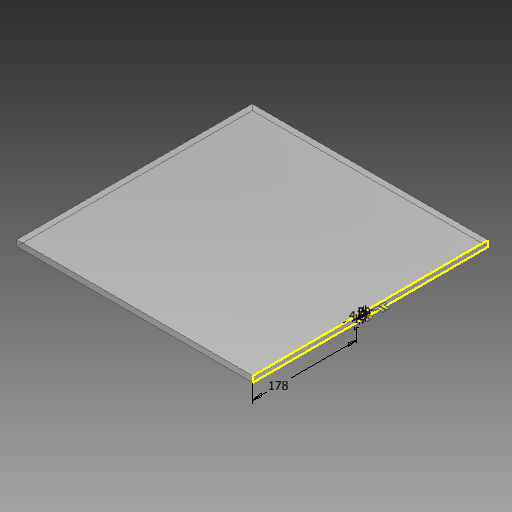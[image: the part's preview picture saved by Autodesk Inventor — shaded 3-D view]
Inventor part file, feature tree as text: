
AUTODESK INVENTOR PART (.ipt)
format: ipt  version: 2018 (Build 220112000, 112)  size: 162,816 bytes
history: native  units: mm
features: extrude x3, sketch x2, pattern_linear x1, projected_geometry x1
ambient origin geometry x8: Origin, YZ Plane, XZ Plane, XY Plane, X Axis, Y Axis, Z Axis, Center Point
bodies: Volumenkörper1 (feature_tree)
feature tree (7):
  extrude  "Extrusion1"  Depth=400.0mm
  sketch  "Skizze2"  dims[d2=10.0mm d3=0.0mm d4=20.0mm d5=1.0mm d6=11.0mm d7=2.0mm d8=4.5mm d10=178.0mm d11=4.0mm d12=0.0mm d15=13.0mm d16=0.0mm d17=20.0mm d19=27.0mm]
  extrude  "Extrusion2"  Depth=20.0mm
  extrude  "Extrusion4"  Depth=1.0mm
  pattern_linear  "Rechteckige Anordnung1"  Spacing1=11.0mm  [1 undecoded]
  sketch  "Skizze1"  dims[d0=400.0mm d1=400.0mm]
  projected_geometry  "Projizierte Kontur1"
note: 1 required parameter value undecoded (feature->parameter linkage not recoverable at this tier; creation-order binding heuristic only, values carry confidence <= 0.55)
